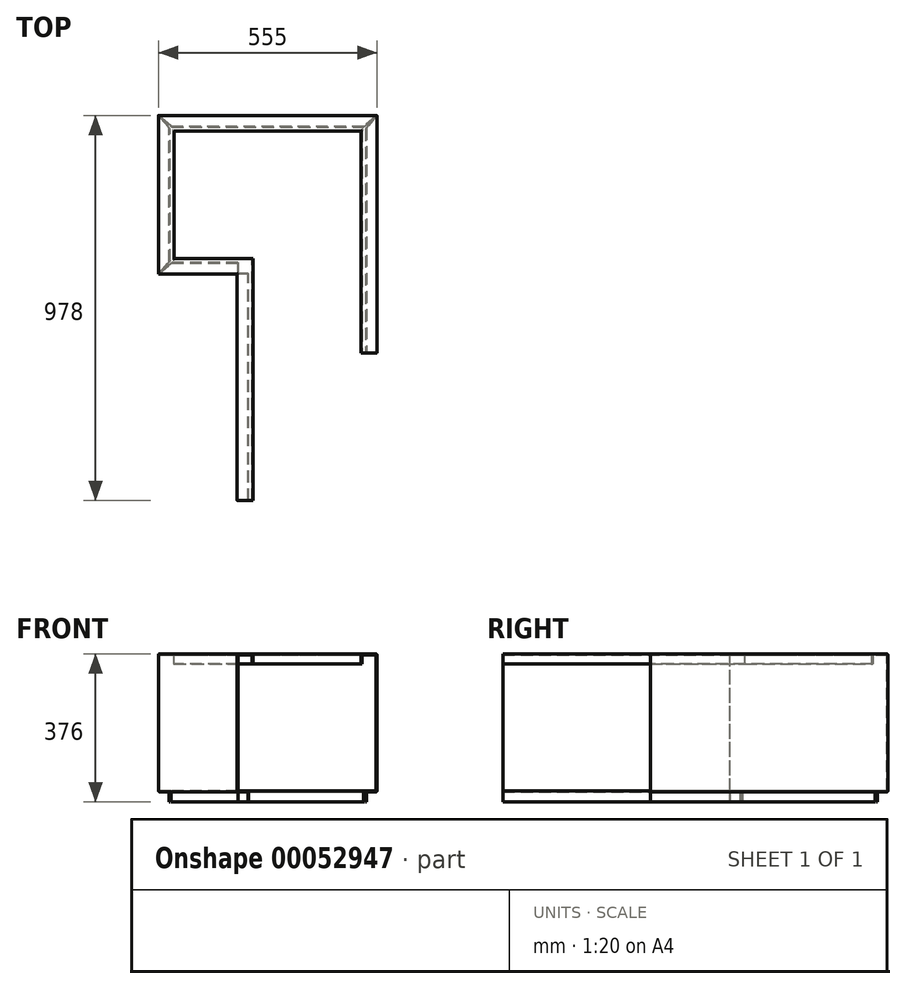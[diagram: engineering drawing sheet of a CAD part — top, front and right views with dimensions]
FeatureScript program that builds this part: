
annotation { "Feature Type Name" : "Feature", "Feature Type Description" : "" }
export const myFeature = defineFeature(function(context is Context, id is Id, definition is map)
    precondition{}
    {
        {
            var Q0;
            Q0=qCreatedBy(makeId("Front.planeOp"),FACE);
            var sketch = newSketch(context, id + "F0", { "sketchPlane" : qUnion([Q0])});
            skLineSegment(sketch, "E0", {"start": v(38, -25) * mm, "end": v(38, -4) * mm});
            skLineSegment(sketch, "E1", {"start": v(36, -2) * mm, "end": v(4, -2) * mm});
            skLineSegment(sketch, "E2", {"start": v(2, -4) * mm, "end": v(2, -346) * mm});
            skLineSegment(sketch, "E3", {"start": v(4, -348) * mm, "end": v(27, -348) * mm});
            skLineSegment(sketch, "E4", {"start": v(29, -350) * mm, "end": v(29, -376) * mm});
            skLineSegment(sketch, "E5.0", {"start": v(27, -352) * mm, "end": v(27, -376) * mm});
            skLineSegment(sketch, "E5.1", {"start": v(40, -25) * mm, "end": v(40, -2) * mm});
            skLineSegment(sketch, "E5.2", {"start": v(38, 0) * mm, "end": v(2, 0) * mm});
            skLineSegment(sketch, "E5.3", {"start": v(0, -2) * mm, "end": v(0, -348) * mm});
            skLineSegment(sketch, "E5.4", {"start": v(2, -350) * mm, "end": v(25, -350) * mm});
            skLineSegment(sketch, "E6", {"start": v(27, -376) * mm, "end": v(29, -376) * mm});
            skLineSegment(sketch, "E7", {"start": v(38, -25) * mm, "end": v(40, -25) * mm});
            skPoint(sketch, "E8.visualSharp", {"position": v(0, 0) * mm});
            skArc(sketch, "E8.filletArc", {"start": v(2, 0) * mm, "mid": v(0.59, -0.59) * mm, "end": v(0, -2) * mm});
            skArc(sketch, "E9.filletArc", {"start": v(4, -2) * mm, "mid": v(2.59, -2.59) * mm, "end": v(2, -4) * mm});
            skPoint(sketch, "E10.visualSharp", {"position": v(40, 0) * mm});
            skArc(sketch, "E10.filletArc", {"start": v(40, -2) * mm, "mid": v(39.41, -0.59) * mm, "end": v(38, 0) * mm});
            skArc(sketch, "E11.filletArc", {"start": v(38, -4) * mm, "mid": v(37.41, -2.59) * mm, "end": v(36, -2) * mm});
            skPoint(sketch, "E12.visualSharp", {"position": v(2, -348) * mm});
            skArc(sketch, "E12.filletArc", {"start": v(2, -346) * mm, "mid": v(2.59, -347.41) * mm, "end": v(4, -348) * mm});
            skPoint(sketch, "E13.visualSharp", {"position": v(0, -350) * mm});
            skArc(sketch, "E13.filletArc", {"start": v(0, -348) * mm, "mid": v(0.59, -349.41) * mm, "end": v(2, -350) * mm});
            skPoint(sketch, "E14.visualSharp", {"position": v(27, -350) * mm});
            skArc(sketch, "E14.filletArc", {"start": v(27, -352) * mm, "mid": v(26.41, -350.59) * mm, "end": v(25, -350) * mm});
            skPoint(sketch, "E15.visualSharp", {"position": v(29, -348) * mm});
            skArc(sketch, "E15.filletArc", {"start": v(29, -350) * mm, "mid": v(28.41, -348.59) * mm, "end": v(27, -348) * mm});
            skSolve(sketch);
        }
        {
            var Q0;
            Q0=qCreatedBy(makeId("Top.planeOp"),FACE);
            var sketch = newSketch(context, id + "F1", { "sketchPlane" : qUnion([Q0])});
            skLineSegment(sketch, "E16", {"start": v(0, 0) * mm, "end": v(0, 575) * mm});
            skLineSegment(sketch, "E17", {"start": v(0, 575) * mm, "end": v(-200, 575) * mm});
            skLineSegment(sketch, "E18", {"start": v(-200, 575) * mm, "end": v(-200, 978) * mm});
            skLineSegment(sketch, "E19", {"start": v(-200, 978) * mm, "end": v(355, 978) * mm});
            skLineSegment(sketch, "E20", {"start": v(355, 978) * mm, "end": v(355, 375) * mm});
            skSolve(sketch);
        }
        {
            var Q0;
            Q0=makeQuery(id+"F0.imprint","IMPRINT",FACE,{"disambiguationData":[TD([[makeQuery(id+"F0.imprint","IMPRINT",EDGE,{"derivedFrom":sQuery(id+"F0.wireOp",EDGE,"E0")}),-1.0]])]});
            var Q1;
            Q1 = qConstructionFilter(qBodyType(qCreatedBy(id + "F1" ,EDGE), BodyType.WIRE), ConstructionObject.NO);
            sweep(context, id + "F2", {"profiles" : qUnion([Q0]), "path" : qUnion([Q1])});
        }
        {
            var Q0;
            Q0=makeQuery(id+"F2.opSweep","SWEPT_FACE",FACE,{"disambiguationData":[OSD([sQuery(id+"F0.wireOp",EDGE,"E3"),sQuery(id+"F1.wireOp",EDGE,"E16")])]});
            var sketch = newSketch(context, id + "F3", { "sketchPlane" : qUnion([Q0])});
            skLineSegment(sketch, "E21", {"start": v(2, 577) * mm, "end": v(2, 605.22) * mm});
            skLineSegment(sketch, "E22", {"start": v(2, 605.22) * mm, "end": v(30.14, 605.22) * mm});
            skLineSegment(sketch, "E23", {"start": v(30.14, 605.22) * mm, "end": v(30.14, 577) * mm});
            skLineSegment(sketch, "E24", {"start": v(30.14, 577) * mm, "end": v(2, 577) * mm});
            skLineSegment(sketch, "E25", {"start": v(-198, 577) * mm, "end": v(-171, 609.18) * mm});
            skLineSegment(sketch, "E26", {"start": v(-171, 609.18) * mm, "end": v(-169.38, 606) * mm});
            skLineSegment(sketch, "E27", {"start": v(-169.38, 606) * mm, "end": v(-165.82, 604) * mm});
            skLineSegment(sketch, "E28", {"start": v(-165.82, 604) * mm, "end": v(-198, 577) * mm});
            skLineSegment(sketch, "E29", {"start": v(-198, 976) * mm, "end": v(-171, 943.82) * mm});
            skLineSegment(sketch, "E30", {"start": v(-171, 943.82) * mm, "end": v(-167.14, 945) * mm});
            skLineSegment(sketch, "E31", {"start": v(-167.14, 945) * mm, "end": v(-165.82, 949) * mm});
            skLineSegment(sketch, "E32", {"start": v(-165.82, 949) * mm, "end": v(-198, 976) * mm});
            skLineSegment(sketch, "E33", {"start": v(353, 976) * mm, "end": v(320.37, 948.75) * mm});
            skLineSegment(sketch, "E34", {"start": v(320.37, 948.75) * mm, "end": v(325.78, 948.75) * mm});
            skLineSegment(sketch, "E35", {"start": v(325.78, 948.75) * mm, "end": v(325.86, 943.46) * mm});
            skLineSegment(sketch, "E36", {"start": v(325.86, 943.46) * mm, "end": v(353, 976) * mm});
            skSolve(sketch);
        }
        {
            var Q0;
            Q0 = qSketchRegion(id + "F3", true);
            extrude(context, id + "F4", {"entities" : qUnion([Q0]), "operationType" : NewBodyOperationType.REMOVE, "oppositeDirection" : true, "depth" : 30 * mm});
        }
    });
